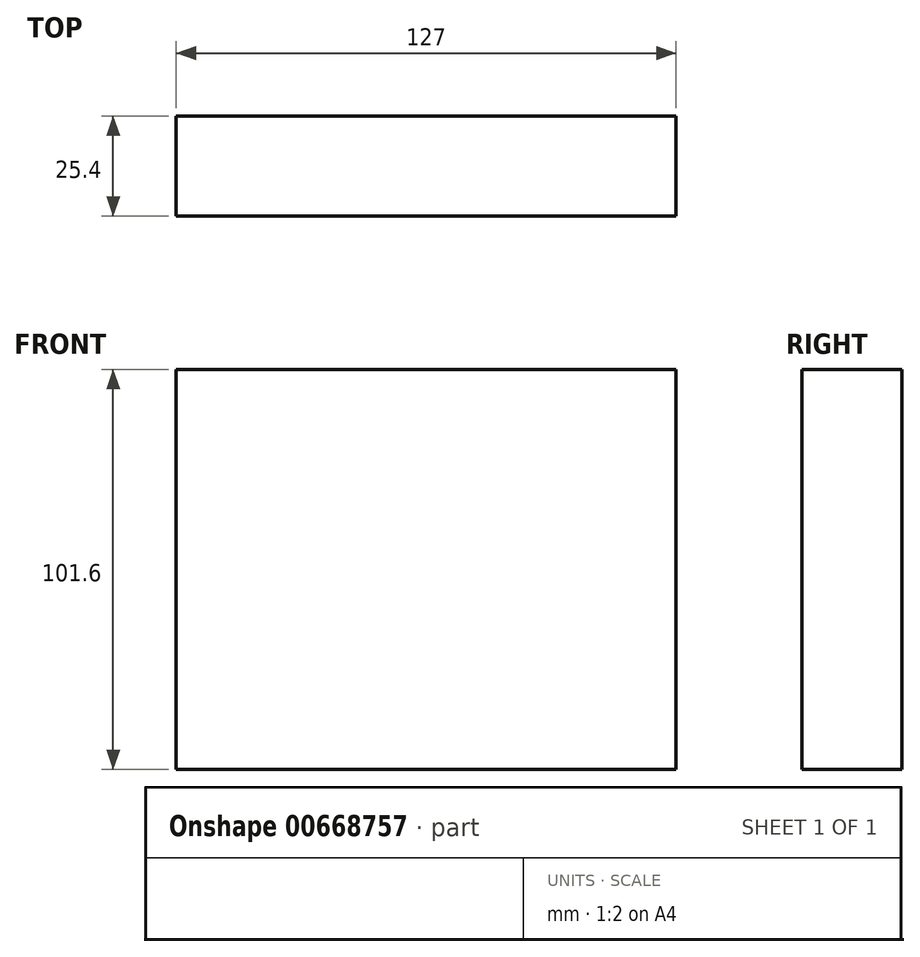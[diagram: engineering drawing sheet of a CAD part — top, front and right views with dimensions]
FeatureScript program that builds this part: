
annotation { "Feature Type Name" : "Feature", "Feature Type Description" : "" }
export const myFeature = defineFeature(function(context is Context, id is Id, definition is map)
    precondition{}
    {
        {
            var Q0;
            Q0=qCreatedBy(makeId("Front.planeOp"),FACE);
            var sketch = newSketch(context, id + "F0", { "sketchPlane" : qUnion([Q0])});
            skLineSegment(sketch, "E0.bottom", {"start": v(-72.54, 63.1) * mm, "end": v(54.46, 63.1) * mm});
            skLineSegment(sketch, "E0.top", {"start": v(-72.54, -38.5) * mm, "end": v(54.46, -38.5) * mm});
            skLineSegment(sketch, "E0.left", {"start": v(-72.54, 63.1) * mm, "end": v(-72.54, -38.5) * mm});
            skLineSegment(sketch, "E0.right", {"start": v(54.46, 63.1) * mm, "end": v(54.46, -38.5) * mm});
            skSolve(sketch);
        }
        {
            var Q0;
            Q0=makeQuery(id+"F0.imprint","IMPRINT",FACE,{"disambiguationData":[TD([[makeQuery(id+"F0.imprint","IMPRINT",EDGE,{"derivedFrom":sQuery(id+"F0.wireOp",EDGE,"E0.bottom")}),-1.0]])]});
            extrude(context, id + "F1", {"entities" : qUnion([Q0]), "depth" : 25.4 * mm, "offsetDistance" : 25.4 * mm});
        }
    });
